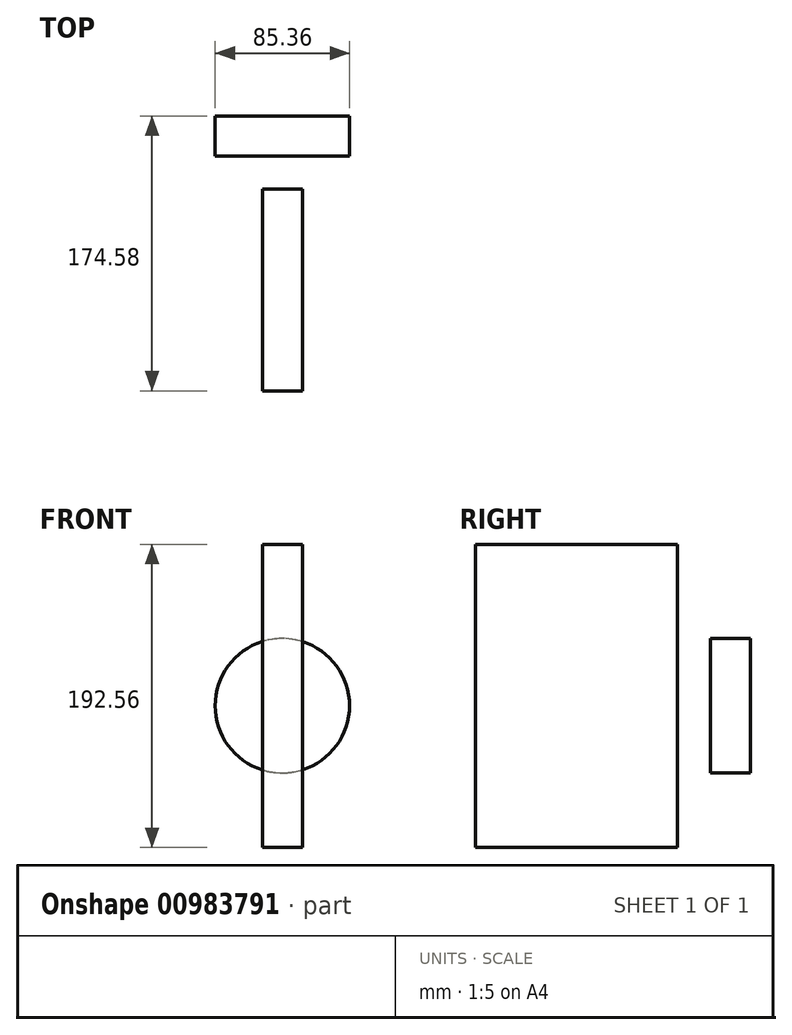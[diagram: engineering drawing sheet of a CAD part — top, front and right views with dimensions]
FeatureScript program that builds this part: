
annotation { "Feature Type Name" : "Feature", "Feature Type Description" : "" }
export const myFeature = defineFeature(function(context is Context, id is Id, definition is map)
    precondition{}
    {
        {
            var Q0;
            Q0=qCreatedBy(makeId("Front.planeOp"),FACE);
            var sketch = newSketch(context, id + "F0", { "sketchPlane" : qUnion([Q0])});
            skCircle(sketch, "E0", {"center": v(0, 0) * mm, "radius": 42.68 * mm});
            skSolve(sketch);
        }
        {
            var Q0;
            Q0=makeQuery(id+"F0.imprint","IMPRINT",FACE,{"disambiguationData":[TD([[makeQuery(id+"F0.imprint","IMPRINT",EDGE,{"derivedFrom":sQuery(id+"F0.wireOp",EDGE,"E0")}),1.0]])]});
            extrude(context, id + "F1", {"entities" : qUnion([Q0]), "depth" : 25.4 * mm, "offsetDistance" : 25.4 * mm});
        }
        {
            var Q0;
            Q0=qCreatedBy(makeId("Right.planeOp"),FACE);
            var sketch = newSketch(context, id + "F2", { "sketchPlane" : qUnion([Q0])});
            skLineSegment(sketch, "E1.bottom", {"start": v(-46.42, 102.5) * mm, "end": v(-174.58, 102.5) * mm});
            skLineSegment(sketch, "E1.top", {"start": v(-46.42, -90.06) * mm, "end": v(-174.58, -90.06) * mm});
            skLineSegment(sketch, "E1.left", {"start": v(-46.42, 102.5) * mm, "end": v(-46.42, -90.06) * mm});
            skLineSegment(sketch, "E1.right", {"start": v(-174.58, 102.5) * mm, "end": v(-174.58, -90.06) * mm});
            skSolve(sketch);
        }
        {
            var Q0;
            Q0=makeQuery(id+"F2.imprint","IMPRINT",FACE,{"disambiguationData":[TD([[makeQuery(id+"F2.imprint","IMPRINT",EDGE,{"derivedFrom":sQuery(id+"F2.wireOp",EDGE,"E1.bottom")}),1.0]])]});
            extrude(context, id + "F3", {"entities" : qUnion([Q0]), "endBound" : BoundingType.SYMMETRIC, "depth" : 25.4 * mm, "offsetDistance" : 25.4 * mm});
        }
        {
            var Q0;
            Q0=qCreatedBy(makeId("Top.planeOp"),FACE);
            cPlane(context, id + "F4", {"entities" : qUnion([Q0]), "cplaneType" : CPlaneType.OFFSET, "offset" : 25.4 * mm, "width" : 152.4 * mm, "height" : 152.4 * mm});
        }
    });
